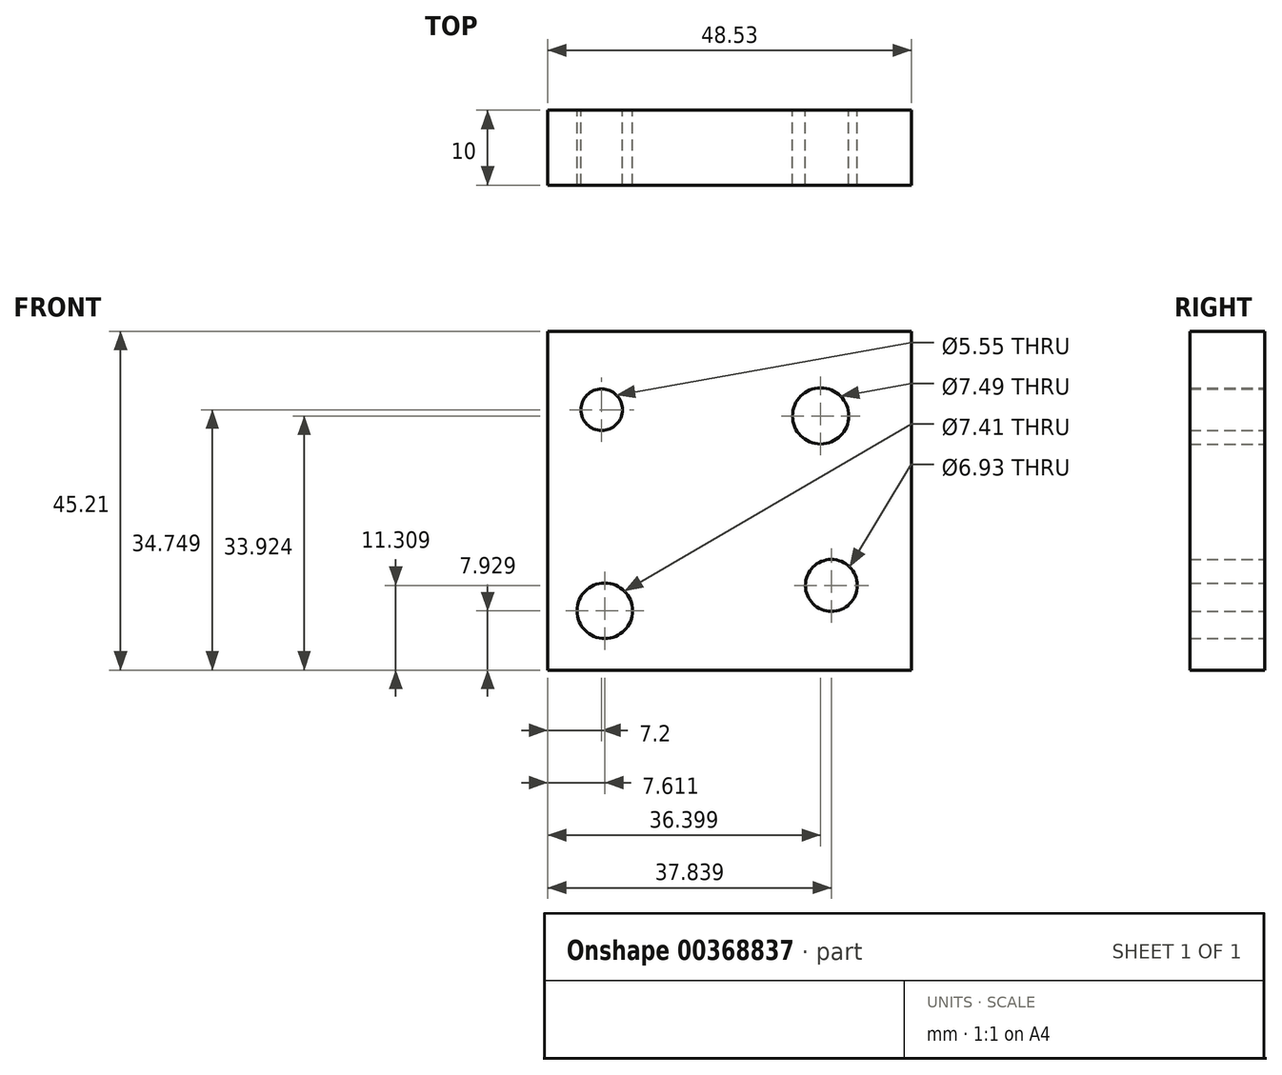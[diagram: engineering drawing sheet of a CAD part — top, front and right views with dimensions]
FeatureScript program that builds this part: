
annotation { "Feature Type Name" : "Feature", "Feature Type Description" : "" }
export const myFeature = defineFeature(function(context is Context, id is Id, definition is map)
    precondition{}
    {
        {
            var Q0;
            Q0=qCreatedBy(makeId("Front.planeOp"),FACE);
            var sketch = newSketch(context, id + "F0", { "sketchPlane" : qUnion([Q0])});
            skLineSegment(sketch, "E0.bottom", {"start": v(-25.53, 16.65) * mm, "end": v(23, 16.65) * mm});
            skLineSegment(sketch, "E0.top", {"start": v(-25.53, -28.56) * mm, "end": v(23, -28.56) * mm});
            skLineSegment(sketch, "E0.left", {"start": v(-25.53, 16.65) * mm, "end": v(-25.53, -28.56) * mm});
            skLineSegment(sketch, "E0.right", {"start": v(23, 16.65) * mm, "end": v(23, -28.56) * mm});
            skCircle(sketch, "E1", {"center": v(-18.33, 6.19) * mm, "radius": 2.78 * mm});
            skCircle(sketch, "E2", {"center": v(10.87, 5.36) * mm, "radius": 3.75 * mm});
            skCircle(sketch, "E3", {"center": v(-17.92, -20.63) * mm, "radius": 3.7 * mm});
            skCircle(sketch, "E4", {"center": v(12.3, -17.25) * mm, "radius": 3.46 * mm});
            skSolve(sketch);
        }
        {
            var Q0;
            Q0=makeQuery(id+"F0.imprint","IMPRINT",FACE,{"disambiguationData":[TD([[makeQuery(id+"F0.imprint","IMPRINT",EDGE,{"derivedFrom":sQuery(id+"F0.wireOp",EDGE,"E0.bottom")}),-1.0]])]});
            extrude(context, id + "F1", {"entities" : qUnion([Q0]), "depth" : 10 * mm});
        }
    });
